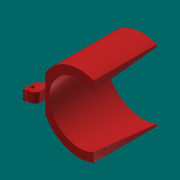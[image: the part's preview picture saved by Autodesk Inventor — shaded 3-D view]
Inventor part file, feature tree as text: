
AUTODESK INVENTOR PART (.ipt)
format: ipt  version: 2013 (Build 170138000, 138)  size: 250,880 bytes
history: native  units: mm
features: sketch x13, extrude x12, other x4, revolve x1, mirror x1, chamfer x1, fillet x1
ambient origin geometry x8: Origin, YZ Plane, XZ Plane, XY Plane, X Axis, Y Axis, Z Axis, Center Point
feature tree (33):
  other  "ソリッド1"
  revolve  "回転1"
  other  "作業平面4"
  sketch  "スケッチ2"
  extrude  "押し出し1"  Depth=32.0mm
  extrude  "押し出し2"  Depth=30.0mm
  extrude  "押し出し3"  Depth=35.0mm
  extrude  "押し出し4"  Depth=2.0mm
  extrude  "押し出し5"  Depth=80.0mm
  mirror  "ミラー1"
  other  "作業平面5"
  extrude  "押し出し7"  TaperAngle=90.0deg  [1 undecoded]
  other  "作業平面6"
  extrude  "押し出し9"  Depth=37.0mm
  extrude  "押し出し10"  Depth=66.0mm
  extrude  "押し出し11"  Depth=46.0mm
  extrude  "押し出し12"  Depth=27.0mm
  extrude  "押し出し13"  Depth=10.0mm
  chamfer  "面取り1"  Distance=40.0mm
  fillet  "フィレット2"  Radius=50.8mm
  extrude  "押し出し14"  Depth=10.0mm TaperAngle=0.0deg
  sketch  "スケッチ1"
  sketch  "スケッチ4"
  sketch  "スケッチ5"
  sketch  "スケッチ6"
  sketch  "スケッチ7"
  sketch  "スケッチ8"
  sketch  "スケッチ9"
  sketch  "スケッチ10"
  sketch  "スケッチ11"
  sketch  "スケッチ12"
  sketch  "スケッチ13"
  sketch  "スケッチ14"
note: 1 required parameter value undecoded (feature->parameter linkage not recoverable at this tier; creation-order binding heuristic only, values carry confidence <= 0.55)
